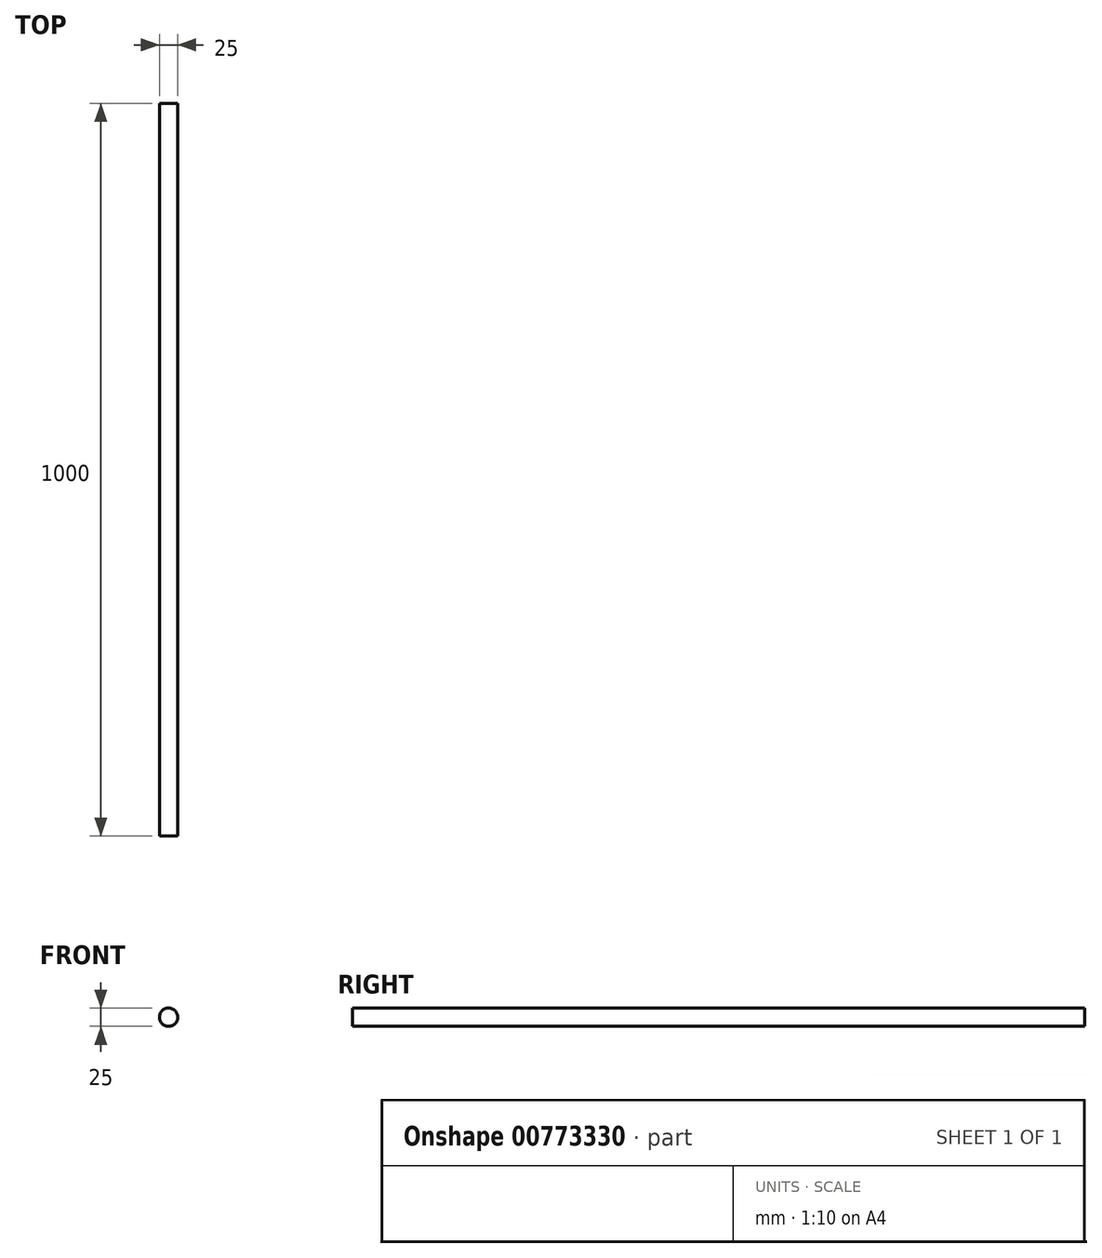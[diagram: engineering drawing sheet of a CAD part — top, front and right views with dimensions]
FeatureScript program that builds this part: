
annotation { "Feature Type Name" : "Feature", "Feature Type Description" : "" }
export const myFeature = defineFeature(function(context is Context, id is Id, definition is map)
    precondition{}
    {
        {
            var Q0;
            Q0=qCreatedBy(makeId("Front.planeOp"),FACE);
            var sketch = newSketch(context, id + "F0", { "sketchPlane" : qUnion([Q0])});
            skCircle(sketch, "E0", {"center": v(0, 0) * mm, "radius": 12.5 * mm});
            skSolve(sketch);
        }
        {
            var Q0;
            Q0=makeQuery(id+"F0.imprint","IMPRINT",FACE,{"disambiguationData":[TD([[makeQuery(id+"F0.imprint","IMPRINT",EDGE,{"derivedFrom":sQuery(id+"F0.wireOp",EDGE,"E0")}),1.0]])]});
            var Q1;
            Q1=sQuery(id+"F0.wireOp",EDGE,"E0");
            extrude(context, id + "F1", {"entities" : qUnion([Q0]), "bodyType" : ToolBodyType.SURFACE, "surfaceEntities" : qUnion([Q1]), "endBound" : BoundingType.SYMMETRIC, "depth" : 1000 * mm, "offsetDistance" : 25.4 * mm});
        }
    });
